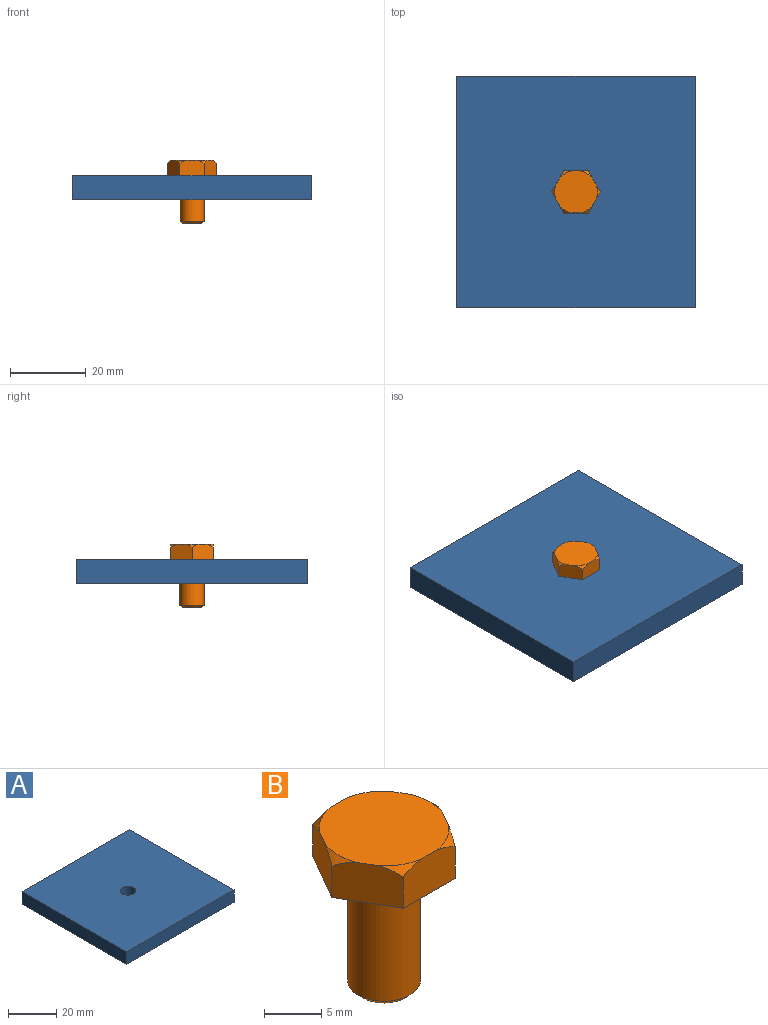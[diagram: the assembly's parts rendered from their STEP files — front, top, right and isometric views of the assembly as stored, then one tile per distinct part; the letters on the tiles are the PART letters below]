
ASSEMBLY  parts=2 mates=1
PART A: 7 faces, bbox 63x61.1x6.4 mm
  f0: plane 61.14x6.35mm, normal (1,0,0), area 388.2mm2, adj f1,f4,f5,f6
  f1: plane 62.96x6.35mm, normal (0,1,0), area 399.8mm2, adj f0,f2,f5,f6
  f2: plane 61.14x6.35mm, normal (-1,0,0), area 388.2mm2, adj f1,f4,f5,f6
  f3: cylinder r=3.17mm len=6.35mm, axis (0,0,1), area 126.7mm2, adj f5,f6
  f4: plane 62.96x6.35mm, normal (0,-1,0), area 399.8mm2, adj f0,f2,f5,f6
  f5: plane 62.96x61.14mm, normal (0,0,-1), area 3817.4mm2, adj f0,f1,f2,f3,f4
  f6: plane 62.96x61.14mm, normal (0,0,1), area 3817.4mm2, adj f0,f1,f2,f3,f4
PART B: 18 faces, bbox 12.9x12.6x16.8 mm
  f0: plane 5.08x5.08mm, normal (0,0,-1), area 20.3mm2, adj f17
  f1: cylinder r=3.17mm len=11.75mm, axis (0,0,-1), area 234.4mm2, adj f16,f17
  f2: plane 12.85x11.13mm, normal (0,0,-1), area 68.9mm2, adj f3,f4,f5,f6,f7,f8,f16
  f3: plane 5.57x4.14mm, normal (0.87,0.5,0), area 25.2mm2, adj f2,f4,f6,f9,f13,f15
  f4: plane 6.43x4.14mm, normal (0,1,0), area 25.2mm2, adj f2,f3,f5,f9,f14,f15
  f5: plane 5.57x4.14mm, normal (-0.87,0.5,0), area 25.2mm2, adj f2,f4,f7,f9,f12,f14
  f6: plane 5.57x4.14mm, normal (0.87,-0.5,0), area 25.2mm2, adj f2,f3,f8,f9,f11,f13
  f7: plane 5.57x4.14mm, normal (-0.87,-0.5,0), area 25.2mm2, adj f2,f5,f8,f9,f10,f12
  f8: plane 6.43x4.14mm, normal (0,-1,0), area 25.2mm2, adj f2,f6,f7,f9,f10,f11
  f9: plane 11.32x11.13mm, normal (0,0,1), area 99.9mm2, adj f3,f4,f5,f6,f7,f8,f10,f11
  f10: cone r=5.66mm half-angle=45deg, axis (0,0,-1), area 1.7mm2, adj f7,f8,f9
  f11: cone r=5.66mm half-angle=45deg, axis (0,0,-1), area 1.7mm2, adj f6,f8,f9
  f12: cone r=5.66mm half-angle=45deg, axis (0,0,-1), area 1.7mm2, adj f5,f7,f9
  f13: cone r=5.66mm half-angle=45deg, axis (0,0,-1), area 1.7mm2, adj f3,f6,f9
  f14: cone r=5.66mm half-angle=45deg, axis (0,0,-1), area 1.7mm2, adj f4,f5,f9
  f15: cone r=5.66mm half-angle=45deg, axis (0,0,-1), area 1.7mm2, adj f3,f4,f9
  f16: torus R=3.49mm, axis (0,0,1), area 10.3mm2, adj f1,f2
  f17: cone r=2.54mm half-angle=45deg, axis (0,0,1), area 16.1mm2, adj f0,f1
PLACE A at identity fixed
PLACE B t=(0,0,-25.4)mm
MATE revolute A.f3 <-> B.f1  axis (0,0,1) through (0,0,0)mm
